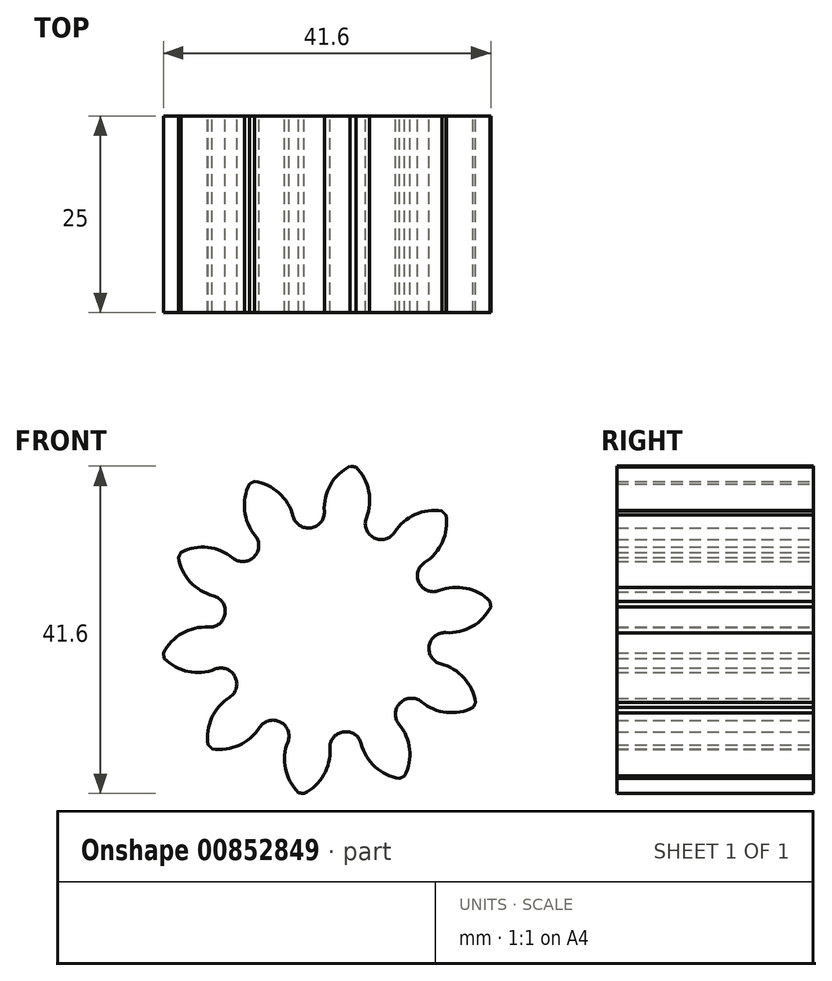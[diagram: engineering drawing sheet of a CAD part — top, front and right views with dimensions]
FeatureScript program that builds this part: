
annotation { "Feature Type Name" : "Feature", "Feature Type Description" : "" }
export const myFeature = defineFeature(function(context is Context, id is Id, definition is map)
    precondition{}
    {
        {
            var Q0;
            Q0=qCreatedBy(makeId("Front.planeOp"),FACE);
            var sketch = newSketch(context, id + "F0", { "sketchPlane" : qUnion([Q0])});
            skCircle(sketch, "E0", {"center": v(0, 0) * mm, "radius": 17.5 * mm, "construction": true});
            skArc(sketch, "E1", {"start": v(-2.03, 12.97) * mm, "mid": v(-2.04, 12.96) * mm, "end": v(-2.05, 12.96) * mm});
            skCircle(sketch, "E2", {"center": v(0, 0) * mm, "radius": 16.45 * mm, "construction": true});
            skLineSegment(sketch, "E3", {"start": v(0, 0) * mm, "end": v(0, 35.56) * mm, "construction": true});
            skLineSegment(sketch, "E4", {"start": v(0, 0) * mm, "end": v(12.83, 35.24) * mm, "construction": true});
            skArc(sketch, "E5", {"start": v(2.93, 20.8) * mm, "mid": v(0.43, 18.42) * mm, "end": v(-0.35, 15.07) * mm});
            skLineSegment(sketch, "E6", {"start": v(0, 0) * mm, "end": v(10.55, 32.47) * mm, "construction": true});
            skLineSegment(sketch, "E7", {"start": v(0, 0) * mm, "end": v(-1.14, 32.77) * mm, "construction": true});
            skArc(sketch, "E8.trimOffspring", {"start": v(4.99, 14.23) * mm, "mid": v(5.28, 17.66) * mm, "end": v(3.64, 20.68) * mm});
            skArc(sketch, "E9.trimOffspring", {"start": v(3.64, 20.68) * mm, "mid": v(3.28, 20.74) * mm, "end": v(2.93, 20.8) * mm});
            skLineSegment(sketch, "E10", {"start": v(0, 0) * mm, "end": v(3.28, 20.74) * mm, "construction": true});
            skLineSegment(sketch, "E11", {"start": v(0, 0) * mm, "end": v(-4.18, 26.35) * mm, "construction": true});
            skPoint(sketch, "E12.visualSharp", {"position": v(0.11, 13.12) * mm});
            skArc(sketch, "E12.filletArc", {"start": v(-2.03, 12.97) * mm, "mid": v(-0.78, 13.7) * mm, "end": v(-0.35, 15.07) * mm});
            skPoint(sketch, "E13.visualSharp", {"position": v(3.95, 12.52) * mm});
            skArc(sketch, "E13.filletArc", {"start": v(4.99, 14.23) * mm, "mid": v(4.98, 12.78) * mm, "end": v(5.94, 11.7) * mm});
            skLineSegment(sketch, "E14", {"start": v(0, 0) * mm, "end": v(11.3, 22.18) * mm, "construction": true});
            skArc(sketch, "E15.trimOffspring", {"start": v(5.96, 11.7) * mm, "mid": v(5.95, 11.7) * mm, "end": v(5.94, 11.7) * mm});
            skPoint(sketch, "E16.1.0", {"position": v(-4.16, 12.45) * mm});
            skArc(sketch, "E16.1.1", {"start": v(-9.86, 18.54) * mm, "mid": v(-10.48, 15.16) * mm, "end": v(-9.14, 11.99) * mm});
            skArc(sketch, "E16.1.2", {"start": v(-4.33, 14.44) * mm, "mid": v(-6.1, 17.39) * mm, "end": v(-9.2, 18.87) * mm});
            skPoint(sketch, "E16.1.3", {"position": v(-7.62, 10.68) * mm});
            skArc(sketch, "E16.1.4", {"start": v(-4.33, 14.44) * mm, "mid": v(-3.49, 13.26) * mm, "end": v(-2.07, 12.96) * mm});
            skArc(sketch, "E16.1.5", {"start": v(-9.27, 9.3) * mm, "mid": v(-8.68, 10.62) * mm, "end": v(-9.14, 11.99) * mm});
            skArc(sketch, "E16.1.6", {"start": v(-9.2, 18.87) * mm, "mid": v(-9.53, 18.71) * mm, "end": v(-9.86, 18.54) * mm});
            skArc(sketch, "E16.1.7", {"start": v(-9.27, 9.3) * mm, "mid": v(-9.27, 9.29) * mm, "end": v(-9.28, 9.28) * mm});
            skArc(sketch, "E16.1.8", {"start": v(-2.05, 12.96) * mm, "mid": v(-2.06, 12.96) * mm, "end": v(-2.07, 12.96) * mm});
            skPoint(sketch, "E16.2.0", {"position": v(-10.68, 7.62) * mm});
            skArc(sketch, "E16.2.1", {"start": v(-18.87, 9.2) * mm, "mid": v(-17.4, 6.1) * mm, "end": v(-14.44, 4.33) * mm});
            skArc(sketch, "E16.2.2", {"start": v(-11.99, 9.14) * mm, "mid": v(-15.16, 10.48) * mm, "end": v(-18.54, 9.86) * mm});
            skPoint(sketch, "E16.2.3", {"position": v(-12.45, 4.16) * mm});
            skArc(sketch, "E16.2.4", {"start": v(-11.99, 9.14) * mm, "mid": v(-10.62, 8.68) * mm, "end": v(-9.3, 9.27) * mm});
            skArc(sketch, "E16.2.5", {"start": v(-12.96, 2.07) * mm, "mid": v(-13.26, 3.49) * mm, "end": v(-14.44, 4.33) * mm});
            skArc(sketch, "E16.2.6", {"start": v(-18.54, 9.86) * mm, "mid": v(-18.71, 9.53) * mm, "end": v(-18.87, 9.2) * mm});
            skArc(sketch, "E16.2.7", {"start": v(-12.96, 2.07) * mm, "mid": v(-12.96, 2.06) * mm, "end": v(-12.96, 2.05) * mm});
            skArc(sketch, "E16.2.8", {"start": v(-9.28, 9.28) * mm, "mid": v(-9.29, 9.27) * mm, "end": v(-9.3, 9.27) * mm});
            skPoint(sketch, "E16.3.0", {"position": v(-13.12, -0.11) * mm});
            skArc(sketch, "E16.3.1", {"start": v(-20.68, -3.64) * mm, "mid": v(-17.65, -5.29) * mm, "end": v(-14.22, -4.99) * mm});
            skArc(sketch, "E16.3.2", {"start": v(-15.07, 0.35) * mm, "mid": v(-18.42, -0.43) * mm, "end": v(-20.8, -2.93) * mm});
            skPoint(sketch, "E16.3.3", {"position": v(-12.52, -3.95) * mm});
            skArc(sketch, "E16.3.4", {"start": v(-15.07, 0.35) * mm, "mid": v(-13.7, 0.78) * mm, "end": v(-12.97, 2.03) * mm});
            skArc(sketch, "E16.3.5", {"start": v(-11.7, -5.94) * mm, "mid": v(-12.78, -4.98) * mm, "end": v(-14.22, -4.99) * mm});
            skArc(sketch, "E16.3.6", {"start": v(-20.8, -2.93) * mm, "mid": v(-20.74, -3.29) * mm, "end": v(-20.68, -3.64) * mm});
            skArc(sketch, "E16.3.7", {"start": v(-11.7, -5.94) * mm, "mid": v(-11.7, -5.95) * mm, "end": v(-11.7, -5.96) * mm});
            skArc(sketch, "E16.3.8", {"start": v(-12.96, 2.05) * mm, "mid": v(-12.97, 2.04) * mm, "end": v(-12.97, 2.03) * mm});
            skPoint(sketch, "E16.4.0", {"position": v(-10.55, -7.8) * mm});
            skArc(sketch, "E16.4.1", {"start": v(-14.59, -15.1) * mm, "mid": v(-11.18, -14.65) * mm, "end": v(-8.58, -12.4) * mm});
            skArc(sketch, "E16.4.2", {"start": v(-12.4, -8.58) * mm, "mid": v(-14.65, -11.18) * mm, "end": v(-15.1, -14.6) * mm});
            skPoint(sketch, "E16.4.3", {"position": v(-7.8, -10.55) * mm});
            skArc(sketch, "E16.4.4", {"start": v(-12.4, -8.58) * mm, "mid": v(-11.54, -7.41) * mm, "end": v(-11.69, -5.98) * mm});
            skArc(sketch, "E16.4.5", {"start": v(-5.98, -11.69) * mm, "mid": v(-7.41, -11.54) * mm, "end": v(-8.58, -12.4) * mm});
            skArc(sketch, "E16.4.6", {"start": v(-15.1, -14.6) * mm, "mid": v(-14.85, -14.85) * mm, "end": v(-14.59, -15.1) * mm});
            skArc(sketch, "E16.4.7", {"start": v(-5.98, -11.69) * mm, "mid": v(-5.97, -11.7) * mm, "end": v(-5.96, -11.7) * mm});
            skArc(sketch, "E16.4.8", {"start": v(-11.7, -5.96) * mm, "mid": v(-11.69, -5.97) * mm, "end": v(-11.69, -5.98) * mm});
            skPoint(sketch, "E16.5.0", {"position": v(-3.95, -12.52) * mm});
            skArc(sketch, "E16.5.1", {"start": v(-2.93, -20.8) * mm, "mid": v(-0.43, -18.42) * mm, "end": v(0.35, -15.07) * mm});
            skArc(sketch, "E16.5.2", {"start": v(-4.99, -14.23) * mm, "mid": v(-5.28, -17.66) * mm, "end": v(-3.64, -20.68) * mm});
            skPoint(sketch, "E16.5.3", {"position": v(-0.11, -13.12) * mm});
            skArc(sketch, "E16.5.4", {"start": v(-4.99, -14.23) * mm, "mid": v(-4.98, -12.78) * mm, "end": v(-5.94, -11.7) * mm});
            skArc(sketch, "E16.5.5", {"start": v(2.03, -12.97) * mm, "mid": v(0.78, -13.7) * mm, "end": v(0.35, -15.07) * mm});
            skArc(sketch, "E16.5.6", {"start": v(-3.64, -20.68) * mm, "mid": v(-3.28, -20.74) * mm, "end": v(-2.93, -20.8) * mm});
            skArc(sketch, "E16.5.7", {"start": v(2.03, -12.97) * mm, "mid": v(2.04, -12.96) * mm, "end": v(2.05, -12.96) * mm});
            skArc(sketch, "E16.5.8", {"start": v(-5.96, -11.7) * mm, "mid": v(-5.95, -11.7) * mm, "end": v(-5.94, -11.7) * mm});
            skPoint(sketch, "E16.6.0", {"position": v(4.16, -12.45) * mm});
            skArc(sketch, "E16.6.1", {"start": v(9.86, -18.54) * mm, "mid": v(10.48, -15.16) * mm, "end": v(9.14, -11.99) * mm});
            skArc(sketch, "E16.6.2", {"start": v(4.33, -14.44) * mm, "mid": v(6.1, -17.39) * mm, "end": v(9.2, -18.87) * mm});
            skPoint(sketch, "E16.6.3", {"position": v(7.62, -10.68) * mm});
            skArc(sketch, "E16.6.4", {"start": v(4.33, -14.44) * mm, "mid": v(3.49, -13.26) * mm, "end": v(2.07, -12.96) * mm});
            skArc(sketch, "E16.6.5", {"start": v(9.27, -9.3) * mm, "mid": v(8.68, -10.62) * mm, "end": v(9.14, -11.99) * mm});
            skArc(sketch, "E16.6.6", {"start": v(9.2, -18.87) * mm, "mid": v(9.53, -18.71) * mm, "end": v(9.86, -18.54) * mm});
            skArc(sketch, "E16.6.7", {"start": v(9.27, -9.3) * mm, "mid": v(9.27, -9.29) * mm, "end": v(9.28, -9.28) * mm});
            skArc(sketch, "E16.6.8", {"start": v(2.05, -12.96) * mm, "mid": v(2.06, -12.96) * mm, "end": v(2.07, -12.96) * mm});
            skPoint(sketch, "E16.7.0", {"position": v(10.68, -7.62) * mm});
            skArc(sketch, "E16.7.1", {"start": v(18.87, -9.2) * mm, "mid": v(17.4, -6.1) * mm, "end": v(14.44, -4.33) * mm});
            skArc(sketch, "E16.7.2", {"start": v(11.99, -9.14) * mm, "mid": v(15.16, -10.48) * mm, "end": v(18.54, -9.86) * mm});
            skPoint(sketch, "E16.7.3", {"position": v(12.45, -4.16) * mm});
            skArc(sketch, "E16.7.4", {"start": v(11.99, -9.14) * mm, "mid": v(10.62, -8.68) * mm, "end": v(9.3, -9.27) * mm});
            skArc(sketch, "E16.7.5", {"start": v(12.96, -2.07) * mm, "mid": v(13.26, -3.49) * mm, "end": v(14.44, -4.33) * mm});
            skArc(sketch, "E16.7.6", {"start": v(18.54, -9.86) * mm, "mid": v(18.71, -9.53) * mm, "end": v(18.87, -9.2) * mm});
            skArc(sketch, "E16.7.7", {"start": v(12.96, -2.07) * mm, "mid": v(12.96, -2.06) * mm, "end": v(12.96, -2.05) * mm});
            skArc(sketch, "E16.7.8", {"start": v(9.28, -9.28) * mm, "mid": v(9.29, -9.27) * mm, "end": v(9.3, -9.27) * mm});
            skPoint(sketch, "E16.8.0", {"position": v(13.12, 0.11) * mm});
            skArc(sketch, "E16.8.1", {"start": v(20.68, 3.64) * mm, "mid": v(17.65, 5.29) * mm, "end": v(14.22, 4.99) * mm});
            skArc(sketch, "E16.8.2", {"start": v(15.07, -0.35) * mm, "mid": v(18.42, 0.43) * mm, "end": v(20.8, 2.93) * mm});
            skPoint(sketch, "E16.8.3", {"position": v(12.52, 3.95) * mm});
            skArc(sketch, "E16.8.4", {"start": v(15.07, -0.35) * mm, "mid": v(13.7, -0.78) * mm, "end": v(12.97, -2.03) * mm});
            skArc(sketch, "E16.8.5", {"start": v(11.7, 5.94) * mm, "mid": v(12.78, 4.98) * mm, "end": v(14.22, 4.99) * mm});
            skArc(sketch, "E16.8.6", {"start": v(20.8, 2.93) * mm, "mid": v(20.74, 3.29) * mm, "end": v(20.68, 3.64) * mm});
            skArc(sketch, "E16.8.7", {"start": v(11.7, 5.94) * mm, "mid": v(11.7, 5.95) * mm, "end": v(11.7, 5.96) * mm});
            skArc(sketch, "E16.8.8", {"start": v(12.96, -2.05) * mm, "mid": v(12.97, -2.04) * mm, "end": v(12.97, -2.03) * mm});
            skPoint(sketch, "E16.9.0", {"position": v(10.55, 7.8) * mm});
            skArc(sketch, "E16.9.1", {"start": v(14.59, 15.1) * mm, "mid": v(11.18, 14.65) * mm, "end": v(8.58, 12.4) * mm});
            skArc(sketch, "E16.9.2", {"start": v(12.4, 8.58) * mm, "mid": v(14.65, 11.18) * mm, "end": v(15.1, 14.6) * mm});
            skPoint(sketch, "E16.9.3", {"position": v(7.8, 10.55) * mm});
            skArc(sketch, "E16.9.4", {"start": v(12.4, 8.58) * mm, "mid": v(11.54, 7.41) * mm, "end": v(11.69, 5.98) * mm});
            skArc(sketch, "E16.9.5", {"start": v(5.98, 11.69) * mm, "mid": v(7.41, 11.54) * mm, "end": v(8.58, 12.4) * mm});
            skArc(sketch, "E16.9.6", {"start": v(15.1, 14.6) * mm, "mid": v(14.85, 14.85) * mm, "end": v(14.59, 15.1) * mm});
            skArc(sketch, "E16.9.7", {"start": v(5.98, 11.69) * mm, "mid": v(5.97, 11.7) * mm, "end": v(5.96, 11.7) * mm});
            skArc(sketch, "E16.9.8", {"start": v(11.7, 5.96) * mm, "mid": v(11.69, 5.97) * mm, "end": v(11.69, 5.98) * mm});
            skSolve(sketch);
        }
        {
            var Q0;
            Q0 = qSketchRegion(id + "F0", true);
            extrude(context, id + "F1", {"entities" : qUnion([Q0]), "depth" : 25 * mm, "offsetDistance" : 25 * mm});
        }
    });
